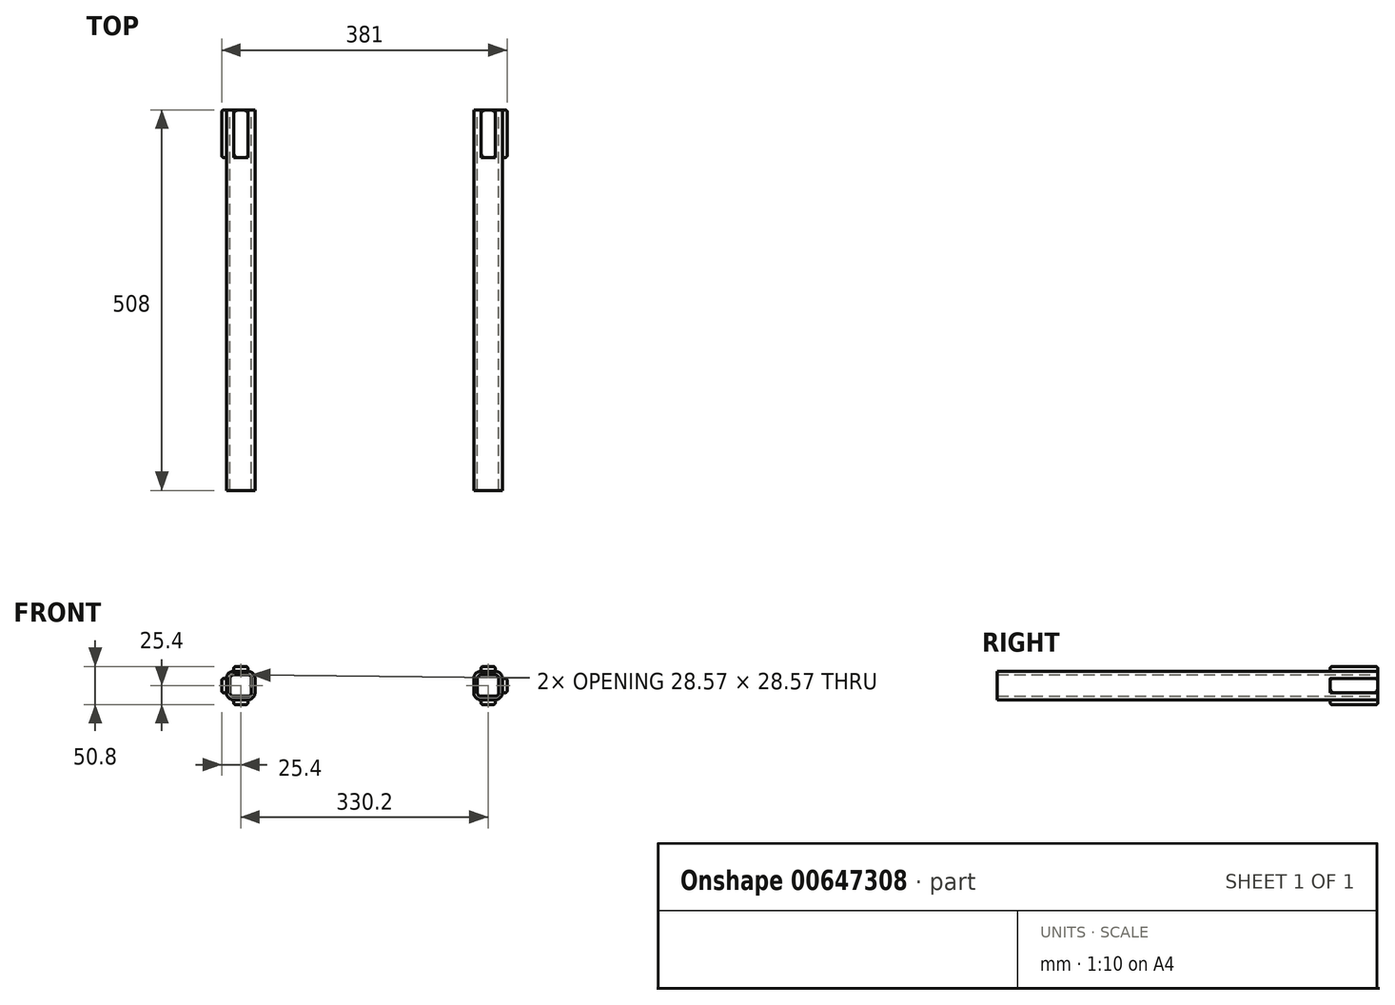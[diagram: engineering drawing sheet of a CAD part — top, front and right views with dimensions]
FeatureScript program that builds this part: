
annotation { "Feature Type Name" : "Feature", "Feature Type Description" : "" }
export const myFeature = defineFeature(function(context is Context, id is Id, definition is map)
    precondition{}
    {
        {
            var Q0;
            Q0=qCreatedBy(makeId("Front.planeOp"),FACE);
            var sketch = newSketch(context, id + "F0", { "sketchPlane" : qUnion([Q0])});
            skLineSegment(sketch, "E0.bottom", {"start": v(-174.62, 19.05) * mm, "end": v(-155.58, 19.05) * mm});
            skLineSegment(sketch, "E0.top", {"start": v(-174.62, -19.05) * mm, "end": v(-155.58, -19.05) * mm});
            skLineSegment(sketch, "E0.left", {"start": v(-184.15, 9.53) * mm, "end": v(-184.15, -9.53) * mm});
            skLineSegment(sketch, "E0.right", {"start": v(-146.05, 9.52) * mm, "end": v(-146.05, -9.52) * mm});
            skPoint(sketch, "E0.middle", {"position": v(0, 0) * mm});
            skPoint(sketch, "E1.visualSharp", {"position": v(-184.15, 19.05) * mm});
            skArc(sketch, "E1.filletArc", {"start": v(-174.62, 19.05) * mm, "mid": v(-181.36, 16.26) * mm, "end": v(-184.15, 9.53) * mm});
            skPoint(sketch, "E2.visualSharp", {"position": v(-146.05, 19.05) * mm});
            skArc(sketch, "E2.filletArc", {"start": v(-146.05, 9.52) * mm, "mid": v(-148.84, 16.26) * mm, "end": v(-155.58, 19.05) * mm});
            skPoint(sketch, "E3.visualSharp", {"position": v(-146.05, -19.05) * mm});
            skArc(sketch, "E3.filletArc", {"start": v(-155.58, -19.05) * mm, "mid": v(-148.84, -16.26) * mm, "end": v(-146.05, -9.52) * mm});
            skPoint(sketch, "E4.visualSharp", {"position": v(-184.15, -19.05) * mm});
            skArc(sketch, "E4.filletArc", {"start": v(-184.15, -9.53) * mm, "mid": v(-181.36, -16.26) * mm, "end": v(-174.62, -19.05) * mm});
            skLineSegment(sketch, "E5.bottom", {"start": v(-174.62, 14.29) * mm, "end": v(-155.58, 14.29) * mm});
            skLineSegment(sketch, "E5.top", {"start": v(-174.62, -14.29) * mm, "end": v(-155.58, -14.29) * mm});
            skLineSegment(sketch, "E5.left", {"start": v(-179.39, 9.52) * mm, "end": v(-179.39, -9.52) * mm});
            skLineSegment(sketch, "E5.right", {"start": v(-150.81, 9.52) * mm, "end": v(-150.81, -9.52) * mm});
            skPoint(sketch, "E5.middle", {"position": v(-179.39, 0) * mm});
            skPoint(sketch, "E6.visualSharp", {"position": v(-179.39, 14.29) * mm});
            skArc(sketch, "E6.filletArc", {"start": v(-174.62, 14.29) * mm, "mid": v(-178, 12.9) * mm, "end": v(-179.39, 9.52) * mm});
            skPoint(sketch, "E7.visualSharp", {"position": v(-150.81, 14.29) * mm});
            skArc(sketch, "E7.filletArc", {"start": v(-150.81, 9.52) * mm, "mid": v(-152.2, 12.9) * mm, "end": v(-155.58, 14.29) * mm});
            skPoint(sketch, "E8.visualSharp", {"position": v(-150.81, -14.29) * mm});
            skArc(sketch, "E8.filletArc", {"start": v(-155.58, -14.29) * mm, "mid": v(-152.2, -12.9) * mm, "end": v(-150.81, -9.52) * mm});
            skPoint(sketch, "E9.visualSharp", {"position": v(-179.39, -14.29) * mm});
            skArc(sketch, "E9.filletArc", {"start": v(-179.39, -9.52) * mm, "mid": v(-178, -12.9) * mm, "end": v(-174.62, -14.29) * mm});
            skLineSegment(sketch, "E10", {"start": v(-179.39, 0) * mm, "end": v(-150.81, 0) * mm, "construction": true});
            skSolve(sketch);
        }
        {
            var Q0;
            Q0=makeQuery(id+"F0.imprint","IMPRINT",FACE,{"disambiguationData":[TD([[makeQuery(id+"F0.imprint","IMPRINT",EDGE,{"derivedFrom":sQuery(id+"F0.wireOp",EDGE,"E0.bottom")}),-1.0]])]});
            extrude(context, id + "F1", {"entities" : qUnion([Q0]), "endBound" : BoundingType.SYMMETRIC, "depth" : 508 * mm, "offsetDistance" : 25.4 * mm});
        }
        {
            var Q0;
            Q0=makeQuery(id+"F1.opExtrude","SWEPT_FACE",FACE,{"disambiguationData":[OSD([sQuery(id+"F0.wireOp",EDGE,"E0.bottom")])]});
            var sketch = newSketch(context, id + "F2", { "sketchPlane" : qUnion([Q0])});
            skLineSegment(sketch, "E11.bottom", {"start": v(-174.62, 254) * mm, "end": v(-155.58, 254) * mm});
            skLineSegment(sketch, "E11.top", {"start": v(-174.62, 190.5) * mm, "end": v(-155.58, 190.5) * mm});
            skLineSegment(sketch, "E11.left", {"start": v(-174.62, 254) * mm, "end": v(-174.62, 190.5) * mm});
            skLineSegment(sketch, "E11.right", {"start": v(-155.58, 254) * mm, "end": v(-155.58, 190.5) * mm});
            skSolve(sketch);
        }
        {
            var Q0;
            Q0 = qSketchRegion(id + "F2", true);
            extrude(context, id + "F3", {"entities" : qUnion([Q0]), "depth" : 6.35 * mm, "offsetDistance" : 25.4 * mm});
        }
        {
            var Q0;
            Q0=makeQuery(id+"F3.opExtrude","CAP_FACE",FACE,{"disambiguationData":[OSD([sQuery(id+"F2.wireOp",EDGE,"E11.bottom"),sQuery(id+"F2.wireOp",EDGE,"E11.top"),sQuery(id+"F2.wireOp",EDGE,"E11.left"),sQuery(id+"F2.wireOp",EDGE,"E11.right")])],"isStart":false});
            fillet(context, id + "F4", {"entities" : qUnion([Q0]), "radius" : 2.54 * mm, "tangentPropagation" : true, "allowEdgeOverflow" : false});
        }
        {
            var Q0;
            Q0=makeQuery(id+"F1.opExtrude","SWEPT_FACE",FACE,{"disambiguationData":[OSD([sQuery(id+"F0.wireOp",EDGE,"E0.left")])]});
            var sketch = newSketch(context, id + "F5", { "sketchPlane" : qUnion([Q0])});
            skLineSegment(sketch, "E12.bottom", {"start": v(-254, 9.53) * mm, "end": v(-190.5, 9.53) * mm});
            skLineSegment(sketch, "E12.top", {"start": v(-254, -9.53) * mm, "end": v(-190.5, -9.53) * mm});
            skLineSegment(sketch, "E12.left", {"start": v(-254, 9.53) * mm, "end": v(-254, -9.53) * mm});
            skLineSegment(sketch, "E12.right", {"start": v(-190.5, 9.53) * mm, "end": v(-190.5, -9.53) * mm});
            skSolve(sketch);
        }
        {
            var Q0;
            Q0 = qSketchRegion(id + "F5", true);
            extrude(context, id + "F6", {"entities" : qUnion([Q0]), "depth" : 6.35 * mm, "offsetDistance" : 25.4 * mm});
        }
        {
            var Q0;
            Q0=makeQuery(id+"F6.opExtrude","CAP_FACE",FACE,{"disambiguationData":[OSD([sQuery(id+"F5.wireOp",EDGE,"E12.bottom"),sQuery(id+"F5.wireOp",EDGE,"E12.top"),sQuery(id+"F5.wireOp",EDGE,"E12.left"),sQuery(id+"F5.wireOp",EDGE,"E12.right")])],"isStart":false});
            fillet(context, id + "F7", {"entities" : qUnion([Q0]), "radius" : 2.54 * mm, "tangentPropagation" : true, "allowEdgeOverflow" : false});
        }
        {
            var Q0;
            Q0=makeQuery(id+"F3.opExtrude","SWEPT_BODY",BODY,{"disambiguationData":[OSD([sQuery(id+"F2.wireOp",EDGE,"E11.bottom"),sQuery(id+"F2.wireOp",EDGE,"E11.top"),sQuery(id+"F2.wireOp",EDGE,"E11.left"),sQuery(id+"F2.wireOp",EDGE,"E11.right")])]});
            var Q1;
            Q1=qCreatedBy(makeId("Top.planeOp"),FACE);
            mirror(context, id + "F8", {"entities" : qUnion([Q0]), "mirrorPlane" : qUnion([Q1])});
        }
        {
            var Q0;
            Q0=makeQuery(id+"F1.opExtrude","SWEPT_BODY",BODY,{"disambiguationData":[OSD([sQuery(id+"F0.wireOp",EDGE,"E0.bottom"),sQuery(id+"F0.wireOp",EDGE,"E0.top"),sQuery(id+"F0.wireOp",EDGE,"E0.left"),sQuery(id+"F0.wireOp",EDGE,"E0.right"),sQuery(id+"F0.wireOp",EDGE,"E1.filletArc"),sQuery(id+"F0.wireOp",EDGE,"E2.filletArc"),sQuery(id+"F0.wireOp",EDGE,"E3.filletArc"),sQuery(id+"F0.wireOp",EDGE,"E4.filletArc"),sQuery(id+"F0.wireOp",EDGE,"E5.bottom"),sQuery(id+"F0.wireOp",EDGE,"E5.top"),sQuery(id+"F0.wireOp",EDGE,"E5.left"),sQuery(id+"F0.wireOp",EDGE,"E5.right"),sQuery(id+"F0.wireOp",EDGE,"E6.filletArc"),sQuery(id+"F0.wireOp",EDGE,"E7.filletArc"),sQuery(id+"F0.wireOp",EDGE,"E8.filletArc"),sQuery(id+"F0.wireOp",EDGE,"E9.filletArc")])]});
            var Q1;
            Q1=makeQuery(id+"F3.opExtrude","SWEPT_BODY",BODY,{"disambiguationData":[OSD([sQuery(id+"F2.wireOp",EDGE,"E11.bottom"),sQuery(id+"F2.wireOp",EDGE,"E11.top"),sQuery(id+"F2.wireOp",EDGE,"E11.left"),sQuery(id+"F2.wireOp",EDGE,"E11.right")])]});
            var Q2;
            Q2=makeQuery(id+"F6.opExtrude","SWEPT_BODY",BODY,{"disambiguationData":[OSD([sQuery(id+"F5.wireOp",EDGE,"E12.bottom"),sQuery(id+"F5.wireOp",EDGE,"E12.top"),sQuery(id+"F5.wireOp",EDGE,"E12.left"),sQuery(id+"F5.wireOp",EDGE,"E12.right")])]});
            var Q3;
            Q3=makeQuery(id+"F8.opPattern","COPY",BODY,{"derivedFrom":makeQuery(id+"F3.opExtrude","SWEPT_BODY",BODY,{"disambiguationData":[OSD([sQuery(id+"F2.wireOp",EDGE,"E11.bottom"),sQuery(id+"F2.wireOp",EDGE,"E11.top"),sQuery(id+"F2.wireOp",EDGE,"E11.left"),sQuery(id+"F2.wireOp",EDGE,"E11.right")])]}),"instanceName":"1"});
            var Q4;
            Q4=qCreatedBy(makeId("Right.planeOp"),FACE);
            mirror(context, id + "F9", {"entities" : qUnion([Q0, Q1, Q2, Q3]), "mirrorPlane" : qUnion([Q4])});
        }
    });
